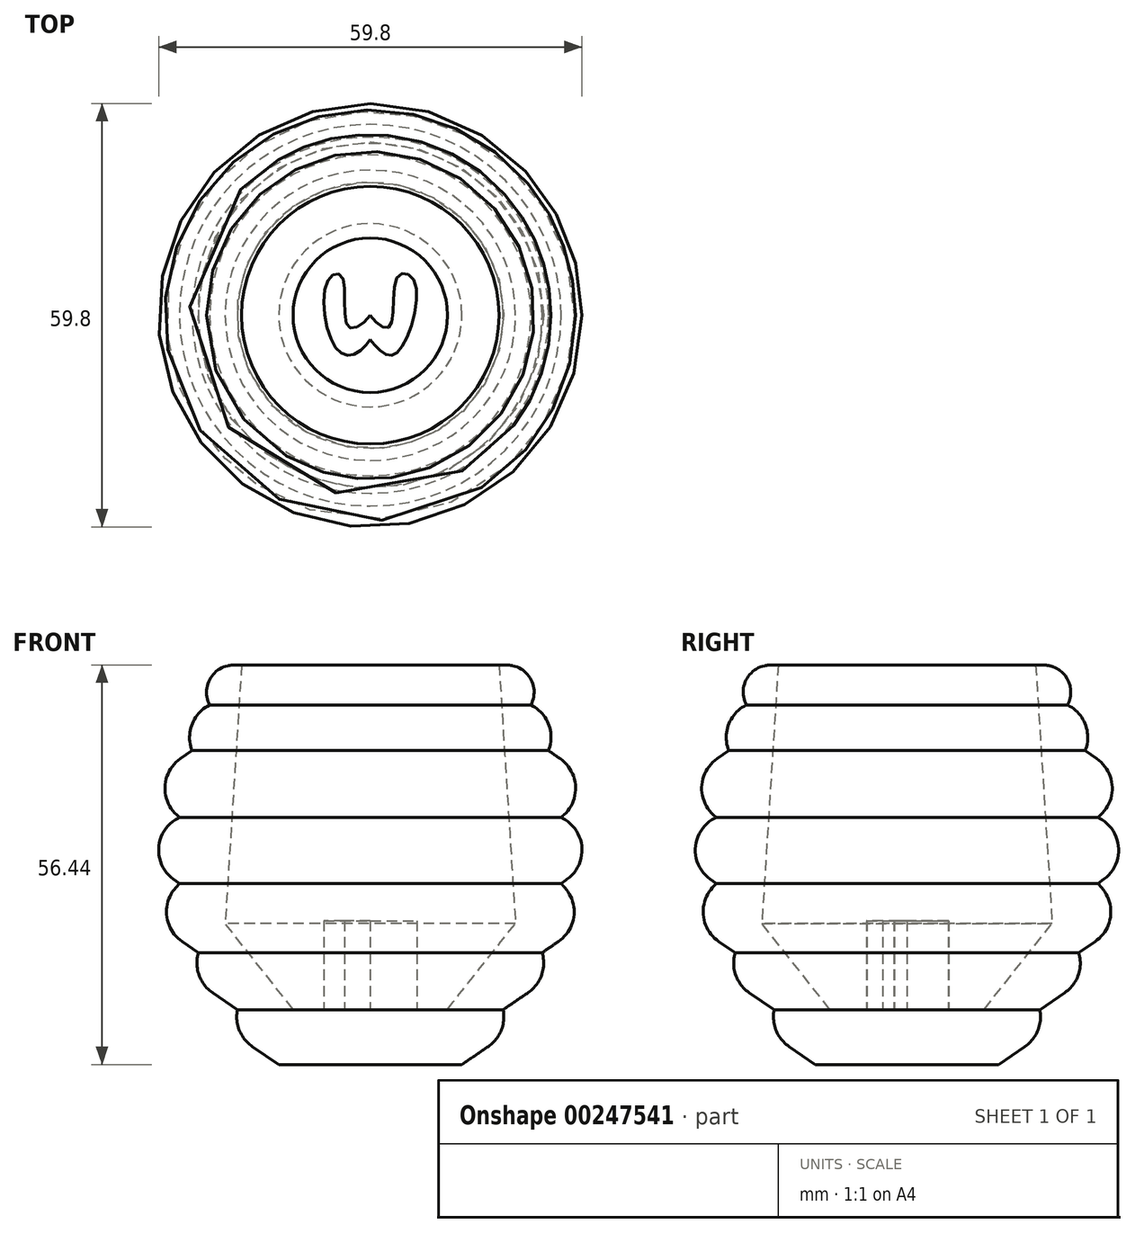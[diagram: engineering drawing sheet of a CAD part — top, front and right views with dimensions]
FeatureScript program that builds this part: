
annotation { "Feature Type Name" : "Feature", "Feature Type Description" : "" }
export const myFeature = defineFeature(function(context is Context, id is Id, definition is map)
    precondition{}
    {
        {
            var Q0;
            Q0=qCreatedBy(makeId("Front.planeOp"),FACE);
            var sketch = newSketch(context, id + "F0", { "sketchPlane" : qUnion([Q0])});
            skLineSegment(sketch, "E0", {"start": v(0, 0) * mm, "end": v(12.8, 0) * mm});
            skLineSegment(sketch, "E1", {"start": v(12.8, 0) * mm, "end": v(12.94, 0) * mm});
            skLineSegment(sketch, "E2", {"start": v(12.94, 0) * mm, "end": v(20.51, 5.17) * mm});
            skLineSegment(sketch, "E3", {"start": v(20.51, 5.17) * mm, "end": v(18.76, 7.74) * mm});
            skLineSegment(sketch, "E4", {"start": v(18.76, 7.74) * mm, "end": v(26.27, 12.87) * mm});
            skLineSegment(sketch, "E5", {"start": v(26.27, 12.87) * mm, "end": v(24.27, 15.8) * mm});
            skLineSegment(sketch, "E6", {"start": v(24.27, 15.8) * mm, "end": v(31.4, 20.67) * mm});
            skLineSegment(sketch, "E7", {"start": v(25.17, 44.34) * mm, "end": v(29.63, 47.32) * mm});
            skLineSegment(sketch, "E8", {"start": v(29.63, 47.32) * mm, "end": v(22.68, 50.8) * mm});
            skLineSegment(sketch, "E9", {"start": v(22.68, 50.8) * mm, "end": v(25.17, 53.53) * mm});
            skLineSegment(sketch, "E10", {"start": v(25.17, 53.53) * mm, "end": v(20.5, 56.44) * mm});
            skLineSegment(sketch, "E11", {"start": v(20.5, 56.44) * mm, "end": v(18.18, 56.44) * mm});
            skLineSegment(sketch, "E12", {"start": v(0, 7.81) * mm, "end": v(0, 0) * mm});
            skLineSegment(sketch, "E13", {"start": v(18.18, 56.44) * mm, "end": v(20.5, 19.94) * mm});
            skLineSegment(sketch, "E14", {"start": v(20.5, 19.94) * mm, "end": v(10.91, 7.81) * mm});
            skLineSegment(sketch, "E15", {"start": v(10.91, 7.81) * mm, "end": v(0, 7.81) * mm});
            skLineSegment(sketch, "E16", {"start": v(31.4, 20.67) * mm, "end": v(26.95, 25.56) * mm});
            skLineSegment(sketch, "E17", {"start": v(34.44, 31.01) * mm, "end": v(26.95, 34.9) * mm});
            skLineSegment(sketch, "E18", {"start": v(26.95, 34.9) * mm, "end": v(32.03, 39.57) * mm});
            skLineSegment(sketch, "E19", {"start": v(32.03, 39.57) * mm, "end": v(25.17, 44.34) * mm});
            skLineSegment(sketch, "E20", {"start": v(26.95, 25.56) * mm, "end": v(34.44, 31.01) * mm});
            skSolve(sketch);
        }
        {
            var Q0;
            Q0=makeQuery(id+"F0.imprint","IMPRINT",FACE,{"disambiguationData":[TD([[makeQuery(id+"F0.imprint","IMPRINT",EDGE,{"derivedFrom":sQuery(id+"F0.wireOp",EDGE,"E0")}),1.0]])]});
            var Q1;
            Q1=sQuery(id+"F0.wireOp",EDGE,"E12");
            revolve(context, id + "F1", {"entities" : qUnion([Q0]), "axis" : qUnion([Q1]), "revolveType" : RevolveType.FULL});
        }
        {
            var Q0;
            Q0=makeQuery(id+"F1.opRevolve","SWEPT_EDGE",EDGE,{"disambiguationData":[OSD([sQuery(id+"F0.wireOp",EDGE,"E7"),sQuery(id+"F0.wireOp",EDGE,"E8")])]});
            fillet(context, id + "F2", {"entities" : qUnion([Q0]), "radius" : 5.08 * mm, "tangentPropagation" : true, "allowEdgeOverflow" : false});
        }
        {
            var Q0;
            Q0=makeQuery(id+"F1.opRevolve","SWEPT_EDGE",EDGE,{"disambiguationData":[OSD([sQuery(id+"F0.wireOp",EDGE,"E10"),sQuery(id+"F0.wireOp",EDGE,"E11")])]});
            fillet(context, id + "F3", {"entities" : qUnion([Q0]), "radius" : 5.08 * mm, "tangentPropagation" : true, "allowEdgeOverflow" : false});
        }
        {
            var Q0;
            Q0=makeQuery(id+"F1.opRevolve","SWEPT_EDGE",EDGE,{"disambiguationData":[OSD([sQuery(id+"F0.wireOp",EDGE,"E4"),sQuery(id+"F0.wireOp",EDGE,"E5")])]});
            fillet(context, id + "F4", {"entities" : qUnion([Q0]), "radius" : 5.08 * mm, "tangentPropagation" : true, "allowEdgeOverflow" : false});
        }
        {
            var Q0;
            Q0=makeQuery(id+"F1.opRevolve","SWEPT_EDGE",EDGE,{"disambiguationData":[OSD([sQuery(id+"F0.wireOp",EDGE,"E2"),sQuery(id+"F0.wireOp",EDGE,"E3")])]});
            fillet(context, id + "F5", {"entities" : qUnion([Q0]), "radius" : 5.08 * mm, "tangentPropagation" : true, "allowEdgeOverflow" : false});
        }
        {
            var Q0;
            Q0=makeQuery(id+"F1.opRevolve","SWEPT_EDGE",EDGE,{"disambiguationData":[OSD([sQuery(id+"F0.wireOp",EDGE,"E18"),sQuery(id+"F0.wireOp",EDGE,"E19")])]});
            fillet(context, id + "F6", {"entities" : qUnion([Q0]), "radius" : 5.08 * mm, "tangentPropagation" : true, "allowEdgeOverflow" : false});
        }
        {
            var Q0;
            Q0=makeQuery(id+"F1.opRevolve","SWEPT_EDGE",EDGE,{"disambiguationData":[OSD([sQuery(id+"F0.wireOp",EDGE,"E17"),sQuery(id+"F0.wireOp",EDGE,"E20")])]});
            fillet(context, id + "F7", {"entities" : qUnion([Q0]), "radius" : 5.08 * mm, "tangentPropagation" : true, "allowEdgeOverflow" : false});
        }
        {
            var Q0;
            Q0=makeQuery(id+"F1.opRevolve","SWEPT_EDGE",EDGE,{"disambiguationData":[OSD([sQuery(id+"F0.wireOp",EDGE,"E6"),sQuery(id+"F0.wireOp",EDGE,"E16")])]});
            fillet(context, id + "F8", {"entities" : qUnion([Q0]), "radius" : 5.08 * mm, "tangentPropagation" : true, "allowEdgeOverflow" : false});
        }
        {
            var Q0;
            Q0=makeQuery(id+"F1.opRevolve","SWEPT_EDGE",EDGE,{"disambiguationData":[OSD([sQuery(id+"F0.wireOp",EDGE,"E9"),sQuery(id+"F0.wireOp",EDGE,"E10")])]});
            fillet(context, id + "F9", {"entities" : qUnion([Q0]), "radius" : 3.8 * mm, "tangentPropagation" : true, "allowEdgeOverflow" : false});
        }
        {
            var Q0;
            Q0=makeQuery(id+"F1.opRevolve","SWEPT_FACE",FACE,{"disambiguationData":[OSD([sQuery(id+"F0.wireOp",EDGE,"E0"),sQuery(id+"F0.wireOp",EDGE,"E1")])]});
            var sketch = newSketch(context, id + "F10", { "sketchPlane" : qUnion([Q0])});
            skFitSpline(sketch, "E21", {"points": [v(0, 0) * mm, v(-3.1, 1.62) * mm, v(-4, -5.42) * mm, v(-5.9, -5.08) * mm, v(-5.45, 3.63) * mm, v(-2.65, 5.65) * mm, v(0, 3.41) * mm], "startDerivative": vector(-14.81, 22.85) * mm, "endDerivative": vector(11.04, -15.77) * mm});
            skFitSpline(sketch, "E22", {"points": [v(0, 3.41) * mm, v(2.49, 5.65) * mm, v(4.95, 3.63) * mm, v(6.06, -5.08) * mm, v(3.83, -5.42) * mm, v(2.71, 1.62) * mm, v(0, 0) * mm], "startDerivative": vector(11.6, 16.49) * mm, "endDerivative": vector(-15.59, -22.66) * mm});
            skSolve(sketch);
        }
        {
            var Q0;
            Q0=makeQuery(id+"F10.imprint","IMPRINT",FACE,{"disambiguationData":[TD([[makeQuery(id+"F10.imprint","IMPRINT",EDGE,{"derivedFrom":sQuery(id+"F10.wireOp",EDGE,"E21")}),-1.0]])]});
            extrude(context, id + "F11", {"entities" : qUnion([Q0]), "operationType" : NewBodyOperationType.ADD, "oppositeDirection" : true, "depth" : 20.32 * mm});
        }
    });
